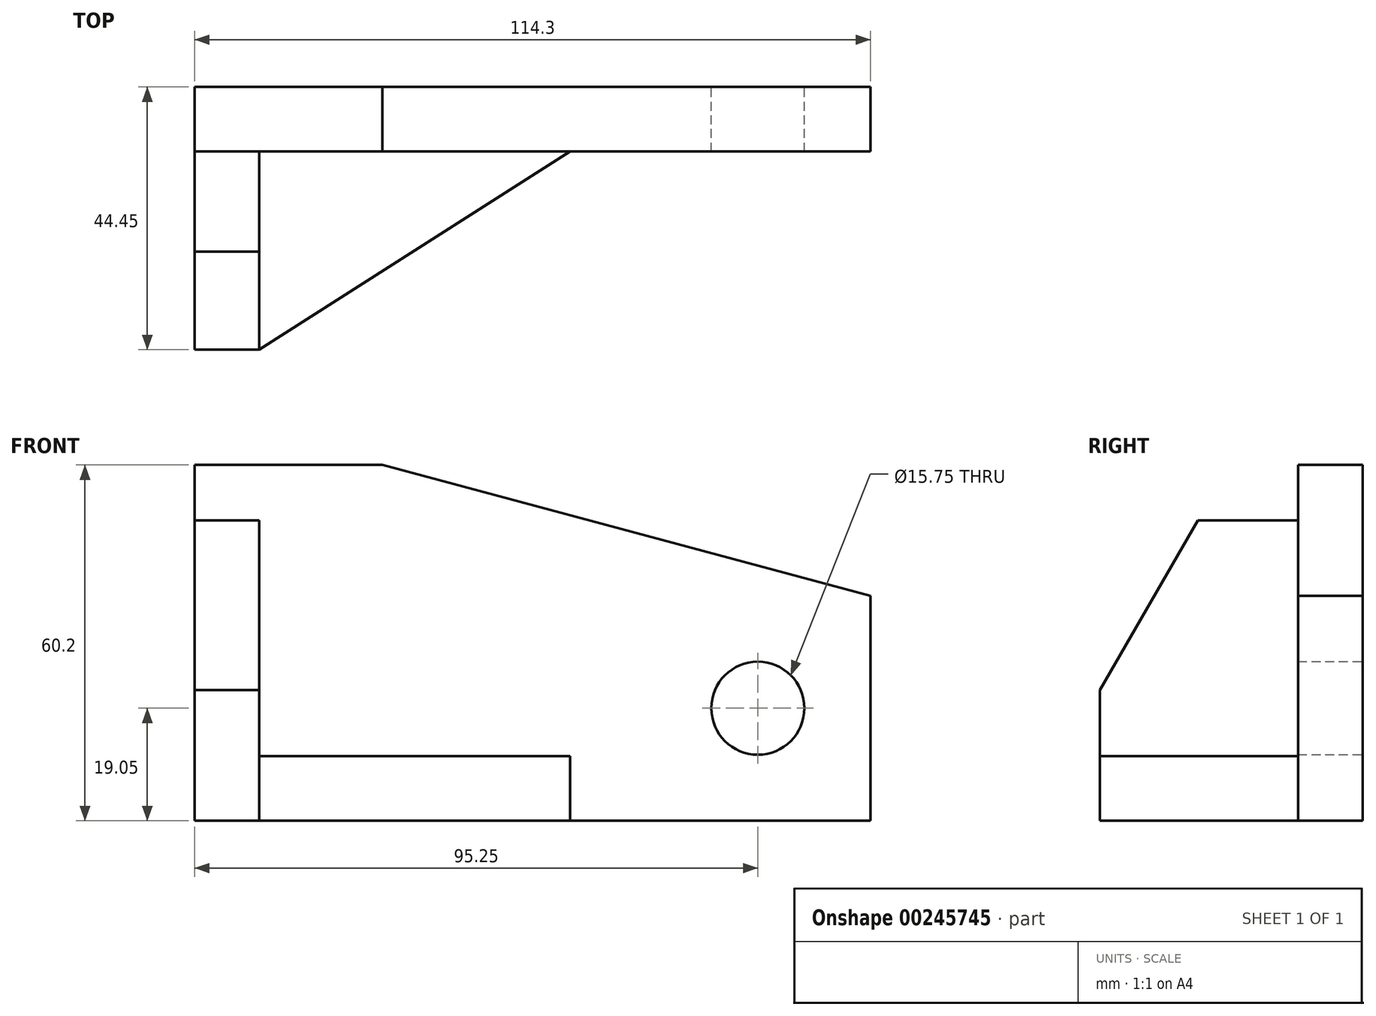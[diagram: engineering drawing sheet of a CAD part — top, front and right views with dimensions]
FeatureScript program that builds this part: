
annotation { "Feature Type Name" : "Feature", "Feature Type Description" : "" }
export const myFeature = defineFeature(function(context is Context, id is Id, definition is map)
    precondition{}
    {
        {
            var Q0;
            Q0=qCreatedBy(makeId("Front.planeOp"),FACE);
            var sketch = newSketch(context, id + "F0", { "sketchPlane" : qUnion([Q0])});
            skLineSegment(sketch, "E0", {"start": v(-56.01, 41.15) * mm, "end": v(-56.01, -19.05) * mm});
            skLineSegment(sketch, "E1", {"start": v(-56.01, -19.05) * mm, "end": v(58.29, -19.05) * mm});
            skLineSegment(sketch, "E2", {"start": v(58.29, -19.05) * mm, "end": v(58.29, 19.03) * mm});
            skLineSegment(sketch, "E3", {"start": v(58.29, 19.03) * mm, "end": v(-24.26, 41.15) * mm});
            skLineSegment(sketch, "E4", {"start": v(-24.26, 41.15) * mm, "end": v(-56.01, 41.15) * mm});
            skLineSegment(sketch, "E5", {"start": v(-24.26, 41.15) * mm, "end": v(52.3, 41.15) * mm, "construction": true});
            skCircle(sketch, "E6", {"center": v(39.24, 0) * mm, "radius": 7.87 * mm});
            skSolve(sketch);
        }
        {
            var Q0;
            Q0 = qSketchRegion(id + "F0", true);
            extrude(context, id + "F1", {"entities" : qUnion([Q0]), "depth" : 10.92 * mm});
        }
        {
            var Q0;
            Q0=makeQuery(id+"F1.opExtrude","SWEPT_FACE",FACE,{"disambiguationData":[OSD([sQuery(id+"F0.wireOp",EDGE,"E1")])]});
            var sketch = newSketch(context, id + "F2", { "sketchPlane" : qUnion([Q0])});
            skLineSegment(sketch, "E7", {"start": v(-56.01, 10.92) * mm, "end": v(-56.01, 44.45) * mm});
            skLineSegment(sketch, "E8", {"start": v(-56.01, 44.45) * mm, "end": v(-45.09, 44.45) * mm});
            skLineSegment(sketch, "E9", {"start": v(-45.09, 44.45) * mm, "end": v(7.49, 10.92) * mm});
            skPoint(sketch, "E10", {"position": v(1.14, 10.92) * mm});
            skSolve(sketch);
        }
        {
            var Q0;
            {var subQ0=sQuery(id+"F2.wireOp",EDGE,"E7");Q0=makeQuery(id+"F2.imprint","IMPRINT",FACE,{"disambiguationData":[TD([[makeQuery(id+"F2.imprint","IMPRINT",EDGE,{"derivedFrom":subQ0}),-1.0]])]});}
            extrude(context, id + "F3", {"entities" : qUnion([Q0]), "oppositeDirection" : true, "depth" : 10.92 * mm});
        }
        {
            var Q0;
            Q0=makeQuery(id+"F3.opExtrude","SWEPT_FACE",FACE,{"disambiguationData":[OSD([sQuery(id+"F2.wireOp",EDGE,"E7")])]});
            var sketch = newSketch(context, id + "F4", { "sketchPlane" : qUnion([Q0])});
            skLineSegment(sketch, "E11", {"start": v(44.45, -8.13) * mm, "end": v(44.45, 3.05) * mm});
            skPoint(sketch, "E11.endSnap0", {"position": v(44.45, -13.59) * mm});
            skLineSegment(sketch, "E12", {"start": v(44.45, 3.05) * mm, "end": v(27.88, 31.75) * mm});
            skLineSegment(sketch, "E13", {"start": v(27.88, 31.75) * mm, "end": v(10.92, 31.75) * mm});
            skLineSegment(sketch, "E14", {"start": v(10.92, 31.75) * mm, "end": v(10.92, -8.13) * mm});
            skLineSegment(sketch, "E15", {"start": v(10.92, -8.13) * mm, "end": v(44.45, -8.13) * mm});
            skSolve(sketch);
        }
        {
            var Q0;
            Q0=makeQuery(id+"F4.imprint","IMPRINT",FACE,{"disambiguationData":[TD([[makeQuery(id+"F4.imprint","IMPRINT",EDGE,{"derivedFrom":sQuery(id+"F4.wireOp",EDGE,"E11")}),1.0]])]});
            extrude(context, id + "F5", {"entities" : qUnion([Q0]), "operationType" : NewBodyOperationType.ADD, "oppositeDirection" : true, "depth" : 10.92 * mm});
        }
    });
